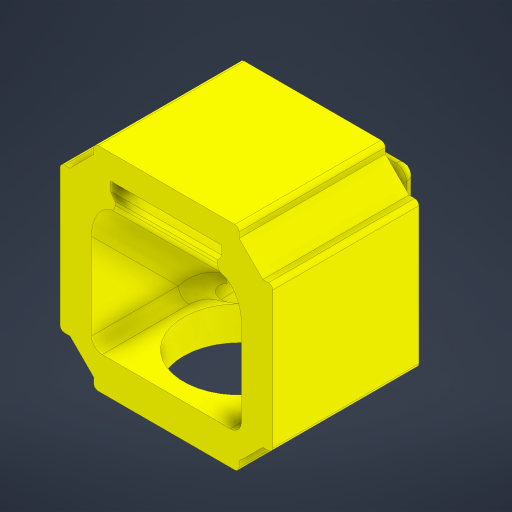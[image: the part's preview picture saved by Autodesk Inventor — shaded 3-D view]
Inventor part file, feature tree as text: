
AUTODESK INVENTOR PART (.ipt)
format: ipt  version: 2023.4 (Build 274418000, 418)  size: 491,008 bytes
history: native  units: mm
features: extrude x8, sketch x5, projected_geometry x5, fillet x3, other x3, plane x1, chamfer x1, reference x1
ambient origin geometry x8: Origin, YZ Plane, XZ Plane, XY Plane, X Axis, Y Axis, Z Axis, Center Point
bodies: Solid1 (feature_tree)
feature tree (27):
  sketch  "Sketch1"  dims[d1=34.15mm d2=0.0mm d3=1.525mm]
  plane  "Work Plane1"
  extrude  "Extrusion1"  Depth=1.525mm
  sketch  "Sketch2"  dims[d4=5.0mm d5=2.5mm]
  extrude  "Extrusion2"  Depth=2.5mm
  extrude  "Extrusion3"  Depth=23.925mm TaperAngle=0.0deg
  extrude  "Extrusion4"  Depth=1.0mm TaperAngle=45.0deg
  chamfer  "Chamfer1"  Distance=1.0mm
  fillet  "Fillet1"  Radius=10.0mm
  extrude  "Extrusion5"  Depth=33.45mm
  sketch  "Sketch4"  dims[d10=35.0mm d11=0.0mm d12=1.0mm d13=2.0mm d14=45.0deg]
  extrude  "Extrusion6"  Depth=33.45mm
  extrude  "Extrusion7"  Depth=26.125mm
  fillet  "Fillet2"  Radius=10.0mm
  extrude  "Extrusion8"  Depth=7.7mm TaperAngle=0.0deg
  fillet  "Fillet3"  Radius=7.7mm
  sketch  "Sketch3"  dims[d6=25.925mm d7=0.0mm d8=23.925mm d9=0.0mm]
  sketch  "Sketch5"  dims[d15=5.5mm d16=1.0mm d18=10.0mm d19=0.0mm d20=33.45mm d21=33.45mm d22=26.125mm d23=10.0mm d24=0.0mm d25=7.7mm d26=0.0mm d27=7.7mm d28=0.0mm d29=2.5mm d30=0.075mm d31=26.125mm]
  projected_geometry  "Projected Loop5"
  reference  "Reference2"
  projected_geometry  "Projected Loop6"
  projected_geometry  "Projected Loop7"
  projected_geometry  "Projected Loop8"
  projected_geometry  "Projected Loop9"
  other  "<path>\Projects\Project Protocube\Protocube\CAD, STL, OBJ Files\1 CAD\Cube 1x1 V5.iam"
  other  "Cube 1x1 V5.iam"
  other  "Cube 1x1 Bottom V5:1"
note: 1 file-system path scrubbed to <path> (originals preserved in map.json)
